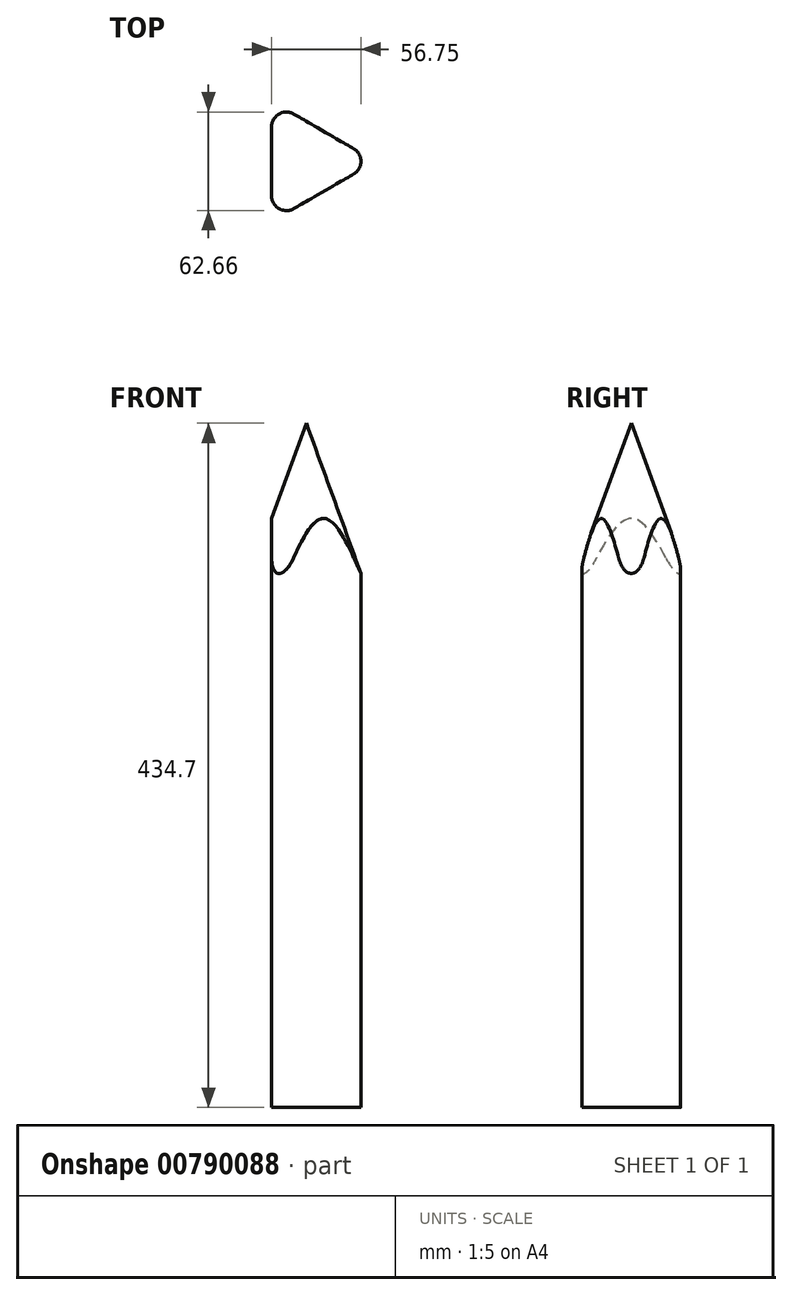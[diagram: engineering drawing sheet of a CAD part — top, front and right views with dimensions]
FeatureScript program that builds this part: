
annotation { "Feature Type Name" : "Feature", "Feature Type Description" : "" }
export const myFeature = defineFeature(function(context is Context, id is Id, definition is map)
    precondition{}
    {
        {
            var Q0;
            Q0=qCreatedBy(makeId("Top.planeOp"),FACE);
            var sketch = newSketch(context, id + "F0", { "sketchPlane" : qUnion([Q0])});
            skCircle(sketch, "E0.cCircle", {"center": v(0, 0) * mm, "radius": 22.02 * mm, "construction": true});
            skLineSegment(sketch, "E0.0", {"start": v(-8.05, 30.08) * mm, "end": v(30.07, 8.07) * mm});
            skLineSegment(sketch, "E0.1", {"start": v(30.07, -8.07) * mm, "end": v(-8.05, -30.08) * mm});
            skLineSegment(sketch, "E0.2", {"start": v(-22.02, -22.01) * mm, "end": v(-22.02, 22.01) * mm});
            skPoint(sketch, "E0.0.midPoint", {"position": v(11.01, 19.07) * mm});
            skPoint(sketch, "E1.visualSharp", {"position": v(-22.02, 38.14) * mm});
            skArc(sketch, "E1.filletArc", {"start": v(-8.05, 30.08) * mm, "mid": v(-17.37, 30.08) * mm, "end": v(-22.02, 22.01) * mm});
            skPoint(sketch, "E2.visualSharp", {"position": v(44.04, 0) * mm});
            skArc(sketch, "E2.filletArc", {"start": v(30.07, -8.07) * mm, "mid": v(34.73, 0) * mm, "end": v(30.07, 8.07) * mm});
            skPoint(sketch, "E3.visualSharp", {"position": v(-22.02, -38.14) * mm});
            skArc(sketch, "E3.filletArc", {"start": v(-22.02, -22.01) * mm, "mid": v(-17.37, -30.08) * mm, "end": v(-8.05, -30.08) * mm});
            skSolve(sketch);
        }
        {
            var Q0;
            Q0 = qSketchRegion(id + "F0", true);
            extrude(context, id + "F1", {"entities" : qUnion([Q0]), "endBound" : BoundingType.SYMMETRIC, "depth" : 526.8 * mm, "offsetDistance" : 25.4 * mm});
        }
        {
            var Q0;
            Q0=qCreatedBy(makeId("Top.planeOp"),FACE);
            cPlane(context, id + "F2", {"entities" : qUnion([Q0]), "cplaneType" : CPlaneType.OFFSET, "offset" : 60.7 * mm, "width" : 152.4 * mm, "height" : 152.4 * mm});
        }
        {
            var Q0;
            Q0=qCreatedBy(id+"F2.planeOp",FACE);
            var sketch = newSketch(context, id + "F3", { "sketchPlane" : qUnion([Q0])});
            skCircle(sketch, "E4", {"center": v(0, 0) * mm, "radius": 42.1 * mm});
            skSolve(sketch);
        }
        {
            var Q0;
            Q0 = qSketchRegion(id + "F3", true);
            extrude(context, id + "F4", {"entities" : qUnion([Q0]), "operationType" : NewBodyOperationType.INTERSECT, "depth" : 143.5 * mm, "offsetDistance" : 25.4 * mm, "hasDraft" : true, "draftAngle" : 20 * degree, "draftPullDirection" : true, "hasSecondDirection" : true, "secondDirectionOppositeDirection" : true, "secondDirectionDepth" : 319.02 * mm});
        }
    });
